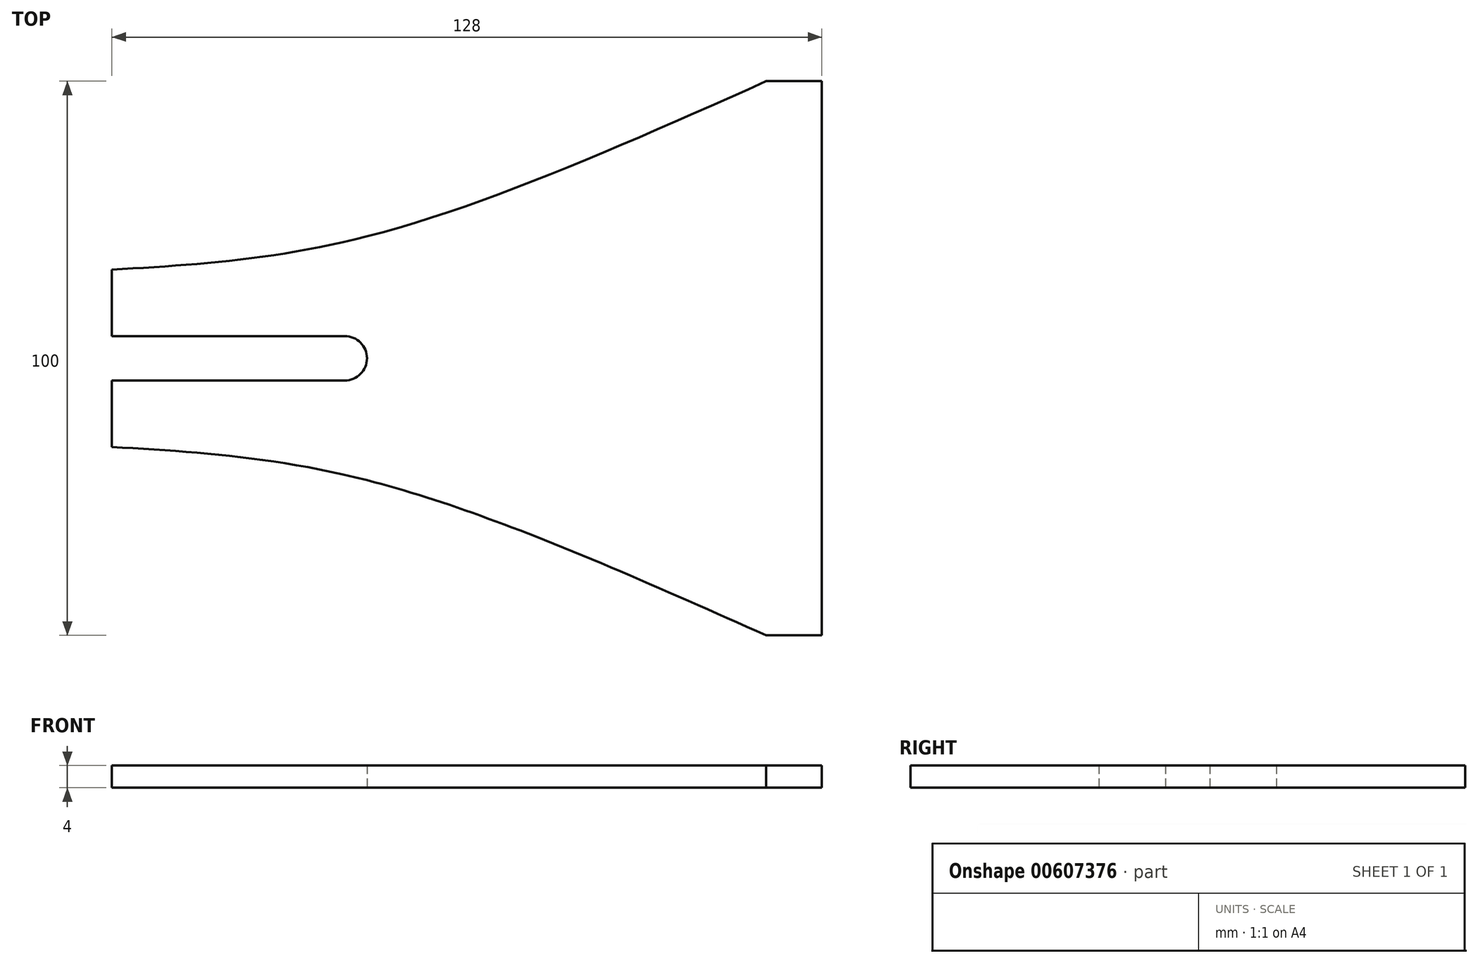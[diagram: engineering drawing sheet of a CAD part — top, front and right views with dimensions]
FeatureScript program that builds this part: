
annotation { "Feature Type Name" : "Feature", "Feature Type Description" : "" }
export const myFeature = defineFeature(function(context is Context, id is Id, definition is map)
    precondition{}
    {
        {
            var Q0;
            Q0=qCreatedBy(makeId("Top.planeOp"),FACE);
            var sketch = newSketch(context, id + "F0", { "sketchPlane" : qUnion([Q0])});
            skLineSegment(sketch, "E0", {"start": v(105.88, 50) * mm, "end": v(105.88, 0) * mm});
            skLineSegment(sketch, "E1", {"start": v(105.88, 0) * mm, "end": v(105.88, -50) * mm});
            skLineSegment(sketch, "E2", {"start": v(105.88, 0) * mm, "end": v(-22.12, 0) * mm});
            skLineSegment(sketch, "E3", {"start": v(-22.12, 4) * mm, "end": v(-22.12, 16) * mm});
            skLineSegment(sketch, "E4", {"start": v(-22.12, -4) * mm, "end": v(-22.12, -16) * mm});
            skLineSegment(sketch, "E5", {"start": v(23.88, -4) * mm, "end": v(23.88, 4) * mm});
            skPoint(sketch, "E6", {"position": v(23.88, 0) * mm});
            skLineSegment(sketch, "E7", {"start": v(23.88, 0) * mm, "end": v(23.88, -22) * mm});
            skLineSegment(sketch, "E8", {"start": v(23.88, 0) * mm, "end": v(23.88, 22) * mm});
            skLineSegment(sketch, "E9", {"start": v(105.88, 50) * mm, "end": v(95.88, 50) * mm});
            skLineSegment(sketch, "E10", {"start": v(105.88, -50) * mm, "end": v(95.88, -50) * mm});
            skFitSpline(sketch, "E11", {"points": [v(-22.12, 16) * mm, v(23.88, 22) * mm, v(95.88, 50) * mm], "startDerivative": vector(100.46, 5.9) * mm, "endDerivative": vector(134.11, 59.83) * mm});
            skFitSpline(sketch, "E12", {"points": [v(-22.12, -16) * mm, v(23.88, -22) * mm, v(95.88, -50) * mm], "startDerivative": vector(100.46, -5.9) * mm, "endDerivative": vector(134.11, -59.83) * mm});
            skLineSegment(sketch, "E13", {"start": v(-22.12, 4) * mm, "end": v(19.88, 4) * mm});
            skLineSegment(sketch, "E14", {"start": v(-22.12, -4) * mm, "end": v(19.88, -4) * mm});
            skLineSegment(sketch, "E15", {"start": v(19.88, 4) * mm, "end": v(19.88, 4) * mm});
            skArc(sketch, "E16", {"start": v(19.88, -4) * mm, "mid": v(23.88, 0) * mm, "end": v(19.88, 4) * mm});
            skPoint(sketch, "E17.end.orphan", {"position": v(105.88, -38.76) * mm});
            skLineSegment(sketch, "E18", {"start": v(105.88, -26.72) * mm, "end": v(55.88, -26.72) * mm});
            skLineSegment(sketch, "E19", {"start": v(55.88, -26.72) * mm, "end": v(55.88, -32.8) * mm});
            skSolve(sketch);
        }
        {
            var Q0;
            Q0 = qSketchRegion(id + "F0", true);
            extrude(context, id + "F1", {"entities" : qUnion([Q0]), "depth" : 4 * mm, "offsetDistance" : 25.4 * mm});
        }
    });
